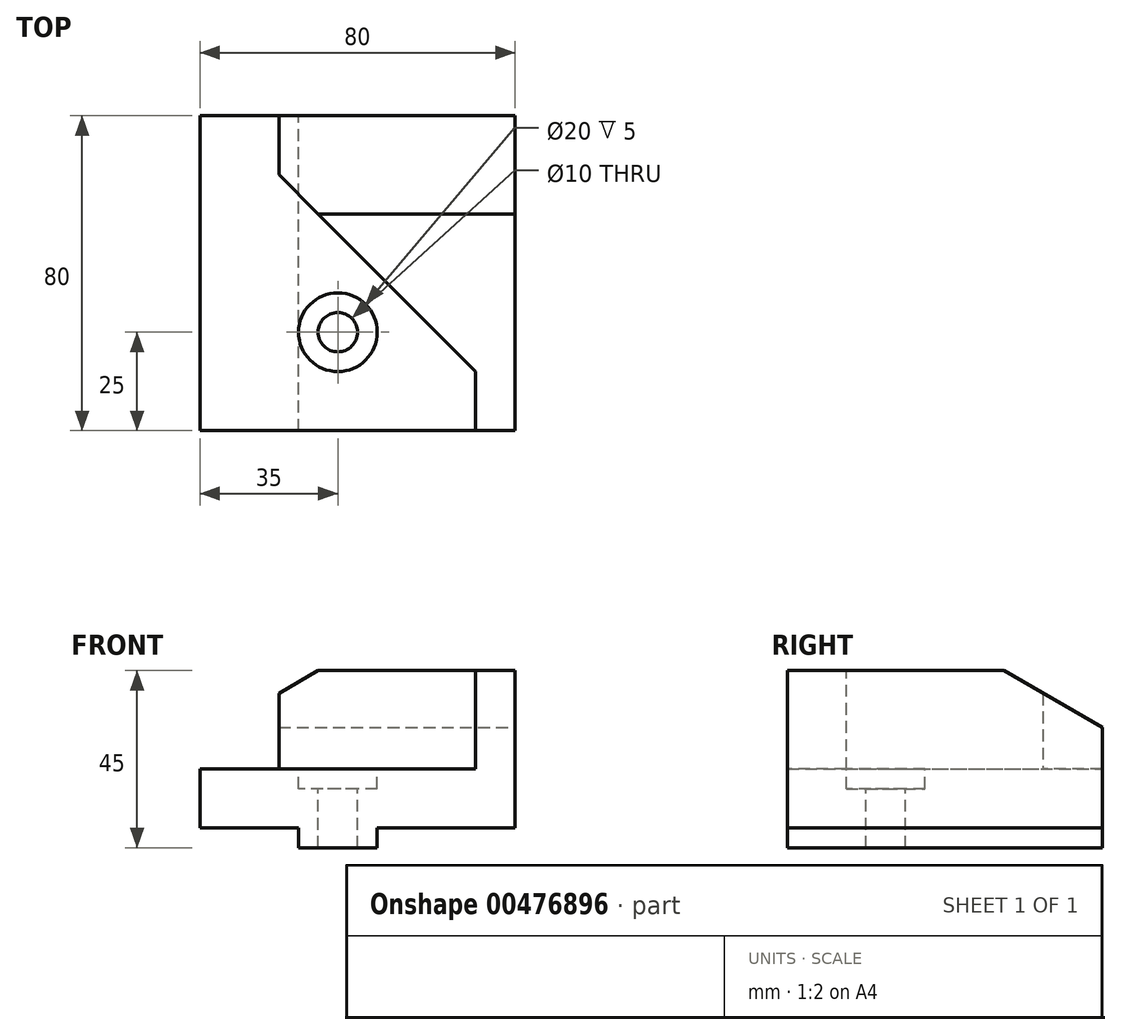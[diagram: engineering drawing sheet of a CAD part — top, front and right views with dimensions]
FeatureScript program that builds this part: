
annotation { "Feature Type Name" : "Feature", "Feature Type Description" : "" }
export const myFeature = defineFeature(function(context is Context, id is Id, definition is map)
    precondition{}
    {
        {
            var Q0;
            Q0=qCreatedBy(makeId("Front.planeOp"),FACE);
            var sketch = newSketch(context, id + "F0", { "sketchPlane" : qUnion([Q0])});
            skLineSegment(sketch, "E0", {"start": v(0, 0) * mm, "end": v(-80, 0) * mm});
            skLineSegment(sketch, "E1", {"start": v(-80, 0) * mm, "end": v(-80, -15) * mm});
            skLineSegment(sketch, "E2", {"start": v(-80, -15) * mm, "end": v(-55, -15) * mm});
            skLineSegment(sketch, "E3", {"start": v(-55, -15) * mm, "end": v(-55, -20) * mm});
            skLineSegment(sketch, "E4", {"start": v(-55, -20) * mm, "end": v(-35, -20) * mm});
            skLineSegment(sketch, "E5", {"start": v(-35, -20) * mm, "end": v(-35, -15) * mm});
            skLineSegment(sketch, "E6", {"start": v(-35, -15) * mm, "end": v(0, -15) * mm});
            skLineSegment(sketch, "E7", {"start": v(0, -15) * mm, "end": v(0, 0) * mm});
            skSolve(sketch);
        }
        {
            var Q0;
            Q0 = qSketchRegion(id + "F0", true);
            extrude(context, id + "F1", {"entities" : qUnion([Q0]), "depth" : 80 * mm});
        }
        {
            var Q0;
            Q0=makeQuery(id+"F1.opExtrude","CAP_FACE",FACE,{"disambiguationData":[OSD([sQuery(id+"F0.wireOp",EDGE,"E0"),sQuery(id+"F0.wireOp",EDGE,"E1"),sQuery(id+"F0.wireOp",EDGE,"E2"),sQuery(id+"F0.wireOp",EDGE,"E3"),sQuery(id+"F0.wireOp",EDGE,"E4"),sQuery(id+"F0.wireOp",EDGE,"E5"),sQuery(id+"F0.wireOp",EDGE,"E6"),sQuery(id+"F0.wireOp",EDGE,"E7")])],"isStart":false});
            var sketch = newSketch(context, id + "F2", { "sketchPlane" : qUnion([Q0])});
            skLineSegment(sketch, "E8", {"start": v(0, 0) * mm, "end": v(-10, 0) * mm});
            skLineSegment(sketch, "E9", {"start": v(0, 0) * mm, "end": v(0, 25) * mm});
            skLineSegment(sketch, "E10", {"start": v(0, 25) * mm, "end": v(-10, 25) * mm});
            skLineSegment(sketch, "E11", {"start": v(-10, 25) * mm, "end": v(-10, 0) * mm});
            skSolve(sketch);
        }
        {
            var Q0;
            Q0 = qSketchRegion(id + "F2", true);
            extrude(context, id + "F3", {"entities" : qUnion([Q0]), "operationType" : NewBodyOperationType.ADD, "oppositeDirection" : true, "depth" : 80 * mm});
        }
        {
            var Q0;
            Q0=makeQuery(id+"F3.opExtrude","SWEPT_FACE",FACE,{"disambiguationData":[OSD([sQuery(id+"F2.wireOp",EDGE,"E10")])]});
            var sketch = newSketch(context, id + "F4", { "sketchPlane" : qUnion([Q0])});
            skLineSegment(sketch, "E12", {"start": v(-10, -65) * mm, "end": v(-50, -25) * mm});
            skLineSegment(sketch, "E13", {"start": v(-10, -25) * mm, "end": v(-50, -25) * mm});
            skLineSegment(sketch, "E14", {"start": v(-10, -65) * mm, "end": v(-10, -25) * mm});
            skSolve(sketch);
        }
        {
            var Q0;
            Q0 = qSketchRegion(id + "F4", true);
            var Q1;
            Q1=makeQuery(id+"F1.opExtrude","SWEPT_FACE",FACE,{"disambiguationData":[OSD([sQuery(id+"F0.wireOp",EDGE,"E0")])]});
            extrude(context, id + "F5", {"entities" : qUnion([Q0]), "operationType" : NewBodyOperationType.ADD, "endBound" : BoundingType.UP_TO_SURFACE, "oppositeDirection" : true, "endBoundEntityFace" : qUnion([Q1]), "depth" : 25 * mm});
        }
        {
            var Q0;
            Q0=makeQuery(id+"F1.opExtrude","SWEPT_FACE",FACE,{"disambiguationData":[OSD([sQuery(id+"F0.wireOp",EDGE,"E0")])]});
            var sketch = newSketch(context, id + "F6", { "sketchPlane" : qUnion([Q0])});
            skLineSegment(sketch, "E15", {"start": v(-50, -25) * mm, "end": v(-60, -15) * mm});
            skLineSegment(sketch, "E16", {"start": v(-60, 0) * mm, "end": v(-60, -15) * mm});
            skLineSegment(sketch, "E17", {"start": v(-60, 0) * mm, "end": v(-10, 0) * mm});
            skLineSegment(sketch, "E18", {"start": v(-10, 0) * mm, "end": v(-10, -25) * mm});
            skLineSegment(sketch, "E19", {"start": v(-10, -25) * mm, "end": v(-50, -25) * mm});
            skSolve(sketch);
        }
        {
            var Q0;
            Q0 = qSketchRegion(id + "F6", true);
            extrude(context, id + "F7", {"entities" : qUnion([Q0]), "operationType" : NewBodyOperationType.ADD, "depth" : 25 * mm});
        }
        {
            var Q0;
            Q0=makeQuery(id+"F3.boolean.opBoolean","MERGE",FACE,{"derivedFrom":[makeQuery(id+"F1.opExtrude","SWEPT_FACE",FACE,{"disambiguationData":[OSD([sQuery(id+"F0.wireOp",EDGE,"E7")])]}),makeQuery(id+"F3.opExtrude","SWEPT_FACE",FACE,{"disambiguationData":[OSD([sQuery(id+"F2.wireOp",EDGE,"E9")])]})]});
            var sketch = newSketch(context, id + "F8", { "sketchPlane" : qUnion([Q0])});
            skLineSegment(sketch, "E20", {"start": v(0, 25) * mm, "end": v(-25, 25) * mm});
            skLineSegment(sketch, "E21", {"start": v(-25, 25) * mm, "end": v(0, 10.57) * mm});
            skLineSegment(sketch, "E22", {"start": v(0, 25) * mm, "end": v(0, 10.57) * mm});
            skSolve(sketch);
        }
        {
            var Q0;
            Q0 = qSketchRegion(id + "F8", true);
            extrude(context, id + "F9", {"entities" : qUnion([Q0]), "operationType" : NewBodyOperationType.REMOVE, "endBound" : BoundingType.THROUGH_ALL, "oppositeDirection" : true, "depth" : 25 * mm});
        }
        {
            var Q0;
            Q0=makeQuery(id+"F1.opExtrude","SWEPT_FACE",FACE,{"disambiguationData":[OSD([sQuery(id+"F0.wireOp",EDGE,"E0")])]});
            var sketch = newSketch(context, id + "F10", { "sketchPlane" : qUnion([Q0])});
            skLineSegment(sketch, "E23", {"start": v(-80, -80) * mm, "end": v(-80, -55) * mm, "construction": true});
            skLineSegment(sketch, "E24", {"start": v(-80, -55) * mm, "end": v(-45, -55) * mm, "construction": true});
            skCircle(sketch, "E25", {"center": v(-45, -55) * mm, "radius": 10 * mm});
            skSolve(sketch);
        }
        {
            var Q0;
            Q0 = qSketchRegion(id + "F10", true);
            extrude(context, id + "F11", {"entities" : qUnion([Q0]), "operationType" : NewBodyOperationType.REMOVE, "oppositeDirection" : true, "depth" : 5 * mm});
        }
        {
            var Q0;
            Q0=makeQuery(id+"F11.boolean.opBoolean","COPY",FACE,{"derivedFrom":makeQuery(id+"F11.opExtrude","CAP_FACE",FACE,{"disambiguationData":[OSD([sQuery(id+"F10.wireOp",EDGE,"E25")])],"isStart":false})});
            var sketch = newSketch(context, id + "F12", { "sketchPlane" : qUnion([Q0])});
            skCircle(sketch, "E26", {"center": v(-45, -55) * mm, "radius": 5 * mm});
            skSolve(sketch);
        }
        {
            var Q0;
            Q0=makeQuery(id+"F12.imprint","IMPRINT",FACE,{"disambiguationData":[TD([[makeQuery(id+"F12.imprint","IMPRINT",EDGE,{"derivedFrom":sQuery(id+"F12.wireOp",EDGE,"E26")}),1.0]])]});
            extrude(context, id + "F13", {"entities" : qUnion([Q0]), "operationType" : NewBodyOperationType.REMOVE, "oppositeDirection" : true, "depth" : 25 * mm});
        }
    });
